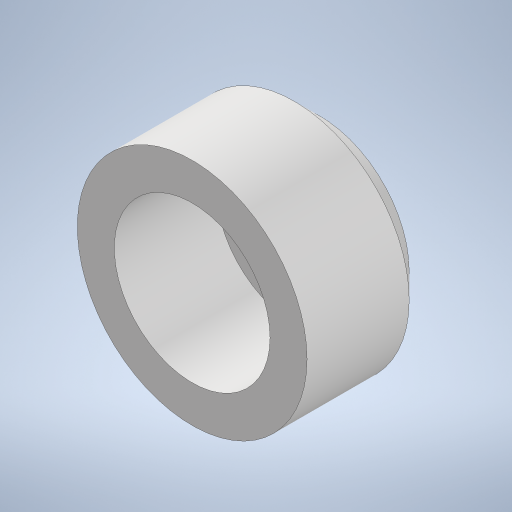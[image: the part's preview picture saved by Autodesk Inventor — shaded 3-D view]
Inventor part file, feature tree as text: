
AUTODESK INVENTOR PART (.ipt)
format: ipt  version: 2024.1 (Build 281209000, 209)  size: 242,176 bytes
history: native  units: in
note: dims shown in document units (in); Inventor stores cm internally (conversion verified against a paired STEP export)
features: extrude x3, sketch x3, chamfer x1, fillet x1
ambient origin geometry x8: Origin, YZ Plane, XZ Plane, XY Plane, X Axis, Y Axis, Z Axis, Center Point
bodies: Solid1 (feature_tree)
feature tree (8):
  extrude  "Extrusion1"  Depth=0.1969in TaperAngle=0.0deg
  extrude  "Extrusion2"  Depth=0.1575in TaperAngle=0.0deg
  chamfer  "Chamfer1"  Distance=0.0394in Angle=45.0deg
  extrude  "Extrusion3"  TaperAngle=0.0deg  [1 undecoded]
  fillet  "Fillet1"  Radius=0.0197in
  sketch  "Sketch1"  dims[d0=0.3543in d1=0.1969in d2=0.0in]
  sketch  "Sketch2"  dims[d3=0.2402in d4=0.1575in d5=0.0in d6=0.0394in d7=0.0787in d8=45.0deg]
  sketch  "Sketch3"  dims[d9=0.0197in d10=0.0in d11=0.0in d12=0.0197in]
note: 1 required parameter value undecoded (feature->parameter linkage not recoverable at this tier; creation-order binding heuristic only, values carry confidence <= 0.55)
